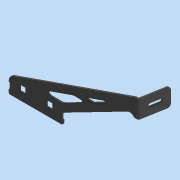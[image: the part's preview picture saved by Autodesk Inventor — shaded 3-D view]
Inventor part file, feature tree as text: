
AUTODESK INVENTOR PART (.ipt)
format: ipt  version: 2020 (Build 240168000, 168)  size: 411,648 bytes
history: native  units: mm
features: other x3, extrude x1, plane x1
ambient origin geometry x8: Origin, YZ Plane, XZ Plane, XY Plane, X Axis, Y Axis, Z Axis, Center Point
bodies: Body1 (feature_tree)
feature tree (5):
  other  "實體1"
  extrude  "擠出1"  Depth=130.0mm
  other  "折彎零件1"
  plane  "工作平面1"
  other  "定義1"
